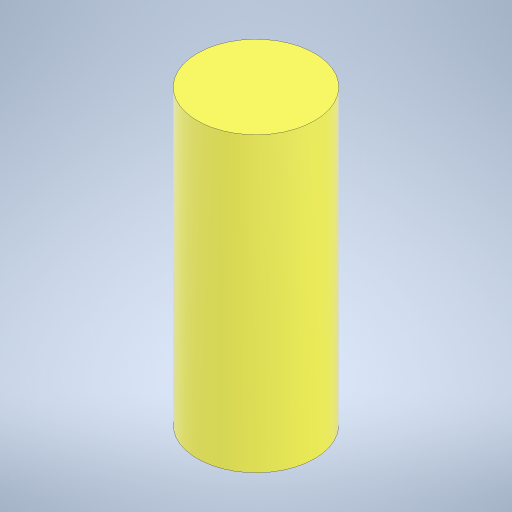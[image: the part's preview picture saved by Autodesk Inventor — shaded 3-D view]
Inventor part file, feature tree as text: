
AUTODESK INVENTOR PART (.ipt)
format: ipt  version: 2024.3 (Build 283343000, 343)  size: 214,016 bytes
history: native  units: mm
features: extrude x1, sketch x1
ambient origin geometry x8: Origin, YZ Plane, XZ Plane, XY Plane, X Axis, Y Axis, Z Axis, Center Point
bodies: Solid1 (feature_tree)
feature tree (2):
  extrude  "Extrusion1"  Depth=10.0mm TaperAngle=0.0deg
  sketch  "Sketch1"  dims[d0=4.0mm d1=10.0mm d2=0.0mm]
